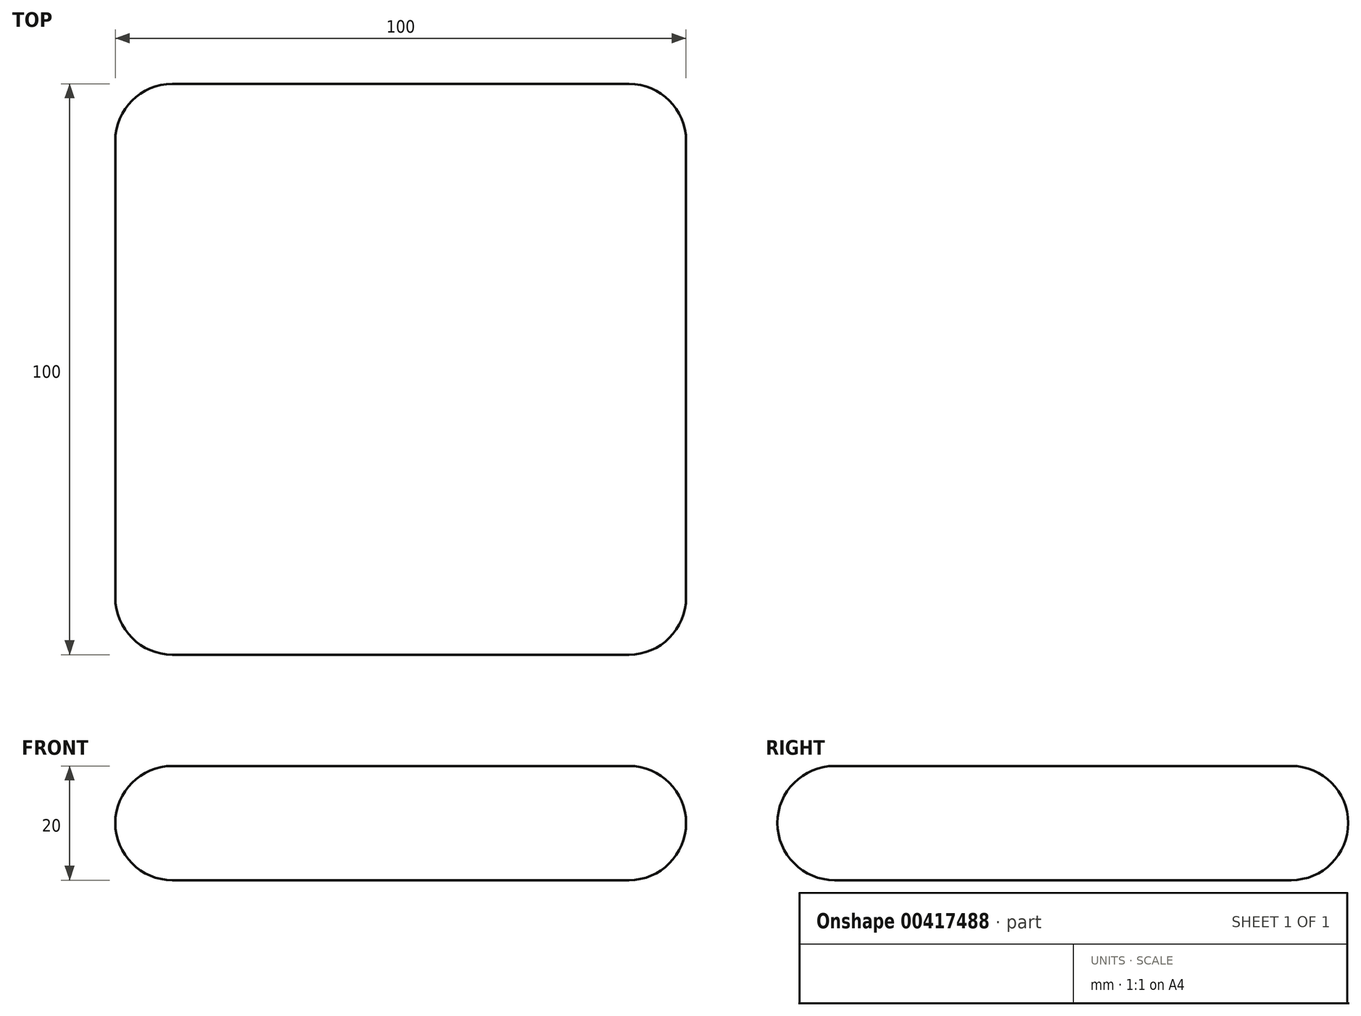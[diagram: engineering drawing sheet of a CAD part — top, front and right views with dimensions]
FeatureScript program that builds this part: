
annotation { "Feature Type Name" : "Feature", "Feature Type Description" : "" }
export const myFeature = defineFeature(function(context is Context, id is Id, definition is map)
    precondition{}
    {
        {
            var Q0;
            Q0=qCreatedBy(makeId("Top.planeOp"),FACE);
            var sketch = newSketch(context, id + "F0", { "sketchPlane" : qUnion([Q0])});
            skLineSegment(sketch, "E0.bottom", {"start": v(0, 0) * mm, "end": v(100, 0) * mm});
            skLineSegment(sketch, "E0.top", {"start": v(0, 100) * mm, "end": v(100, 100) * mm});
            skLineSegment(sketch, "E0.left", {"start": v(0, 0) * mm, "end": v(0, 100) * mm});
            skLineSegment(sketch, "E0.right", {"start": v(100, 0) * mm, "end": v(100, 100) * mm});
            skSolve(sketch);
        }
        {
            var Q0;
            Q0=makeQuery(id+"F0.imprint","IMPRINT",FACE,{"disambiguationData":[TD([[makeQuery(id+"F0.imprint","IMPRINT",EDGE,{"derivedFrom":sQuery(id+"F0.wireOp",EDGE,"E0.bottom")}),1.0]])]});
            extrude(context, id + "F1", {"entities" : qUnion([Q0]), "depth" : 20 * mm});
        }
        {
            var Q0;
            Q0=makeQuery(id+"F1.opExtrude","SWEPT_FACE",FACE,{"disambiguationData":[OSD([sQuery(id+"F0.wireOp",EDGE,"E0.right")])]});
            var Q1;
            Q1=makeQuery(id+"F1.opExtrude","SWEPT_FACE",FACE,{"disambiguationData":[OSD([sQuery(id+"F0.wireOp",EDGE,"E0.top")])]});
            var Q2;
            Q2=makeQuery(id+"F1.opExtrude","SWEPT_FACE",FACE,{"disambiguationData":[OSD([sQuery(id+"F0.wireOp",EDGE,"E0.left")])]});
            var Q3;
            Q3=makeQuery(id+"F1.opExtrude","SWEPT_FACE",FACE,{"disambiguationData":[OSD([sQuery(id+"F0.wireOp",EDGE,"E0.bottom")])]});
            fillet(context, id + "F2", {"entities" : qUnion([Q0, Q1, Q2, Q3]), "radius" : 10 * mm, "tangentPropagation" : true, "allowEdgeOverflow" : false});
        }
    });
